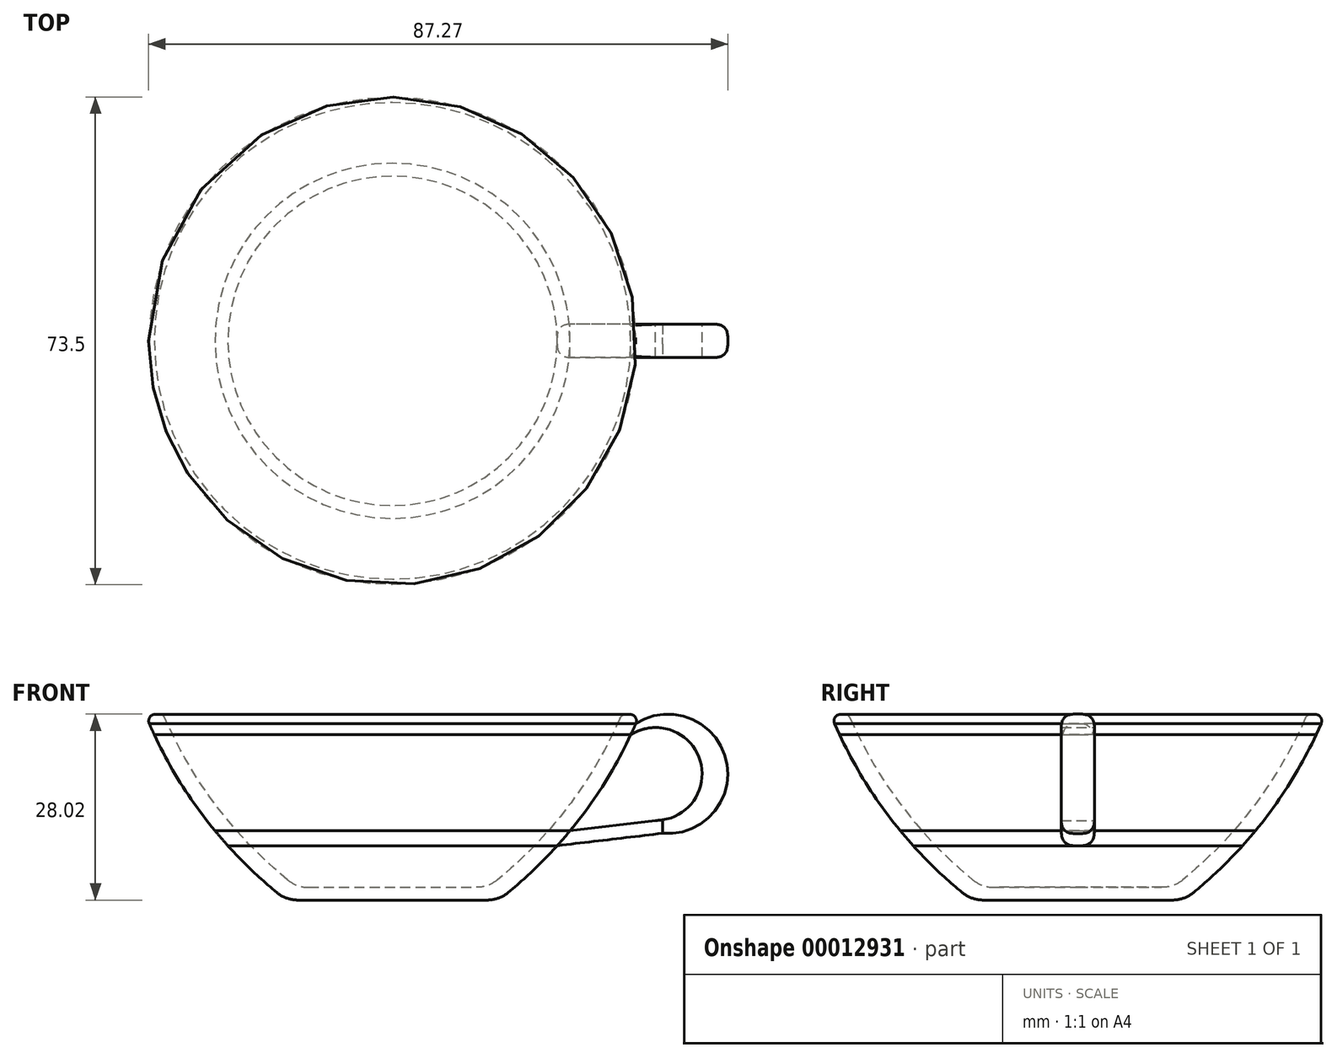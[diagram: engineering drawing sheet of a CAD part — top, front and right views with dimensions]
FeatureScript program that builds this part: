
annotation { "Feature Type Name" : "Feature", "Feature Type Description" : "" }
export const myFeature = defineFeature(function(context is Context, id is Id, definition is map)
    precondition{}
    {
        {
            var Q0;
            Q0=qCreatedBy(makeId("Front.planeOp"),FACE);
            var sketch = newSketch(context, id + "F0", { "sketchPlane" : qUnion([Q0])});
            skLineSegment(sketch, "E0", {"start": v(0, 0) * mm, "end": v(14.25, 0) * mm});
            skArc(sketch, "E1", {"start": v(17.42, 1.13) * mm, "mid": v(21.25, 4.52) * mm, "end": v(24.82, 8.2) * mm});
            skArc(sketch, "E2", {"start": v(15.8, 3.04) * mm, "mid": v(26.49, 14.13) * mm, "end": v(34.29, 27.4) * mm});
            skLineSegment(sketch, "E3", {"start": v(35.75, 28) * mm, "end": v(35.2, 28) * mm});
            skLineSegment(sketch, "E4", {"start": v(0, 0) * mm, "end": v(0, 1.91) * mm});
            skLineSegment(sketch, "E5", {"start": v(0, 1.91) * mm, "end": v(12.64, 1.91) * mm});
            skLineSegment(sketch, "E6", {"start": v(40.7, 10.06) * mm, "end": v(24.82, 8.2) * mm});
            skArc(sketch, "E7", {"start": v(39.61, 12) * mm, "mid": v(46.38, 20.94) * mm, "end": v(35.9, 24.9) * mm});
            skArc(sketch, "E8.trimOffspring", {"start": v(40.7, 10.06) * mm, "mid": v(50.26, 21.16) * mm, "end": v(36.66, 26.6) * mm});
            skLineSegment(sketch, "E9", {"start": v(39.61, 12) * mm, "end": v(26.76, 10.44) * mm});
            skPoint(sketch, "E10.visualSharp", {"position": v(37.25, 28) * mm});
            skArc(sketch, "E10.filletArc", {"start": v(36.66, 26.6) * mm, "mid": v(36.58, 27.55) * mm, "end": v(35.75, 28) * mm});
            skPoint(sketch, "E11.visualSharp", {"position": v(34.54, 28) * mm});
            skArc(sketch, "E11.filletArc", {"start": v(35.2, 28) * mm, "mid": v(34.65, 27.84) * mm, "end": v(34.29, 27.4) * mm});
            skPoint(sketch, "E12.visualSharp", {"position": v(16, 0) * mm});
            skArc(sketch, "E12.filletArc", {"start": v(14.25, 0) * mm, "mid": v(15.93, 0.3) * mm, "end": v(17.42, 1.13) * mm});
            skPoint(sketch, "E13.visualSharp", {"position": v(14.39, 1.91) * mm});
            skArc(sketch, "E13.filletArc", {"start": v(12.64, 1.91) * mm, "mid": v(14.32, 2.2) * mm, "end": v(15.8, 3.04) * mm});
            skArc(sketch, "E14.trimOffspring", {"start": v(26.76, 10.44) * mm, "mid": v(31.79, 17.39) * mm, "end": v(35.9, 24.9) * mm});
            skLineSegment(sketch, "E15", {"start": v(36.66, 26.6) * mm, "end": v(35.9, 24.9) * mm});
            skLineSegment(sketch, "E16", {"start": v(26.76, 10.44) * mm, "end": v(24.82, 8.2) * mm});
            skSolve(sketch);
        }
        {
            var Q0;
            {var subQ6=sQuery(id+"F0.wireOp",EDGE,"E0");Q0=makeQuery(id+"F0.imprint","IMPRINT",FACE,{"disambiguationData":[TD([[makeQuery(id+"F0.imprint","IMPRINT",EDGE,{"derivedFrom":subQ6}),1.0]])]});}
            var Q1;
            Q1=sQuery(id+"F0.wireOp",EDGE,"E4");
            revolve(context, id + "F1", {"entities" : qUnion([Q0]), "axis" : qUnion([Q1]), "revolveType" : RevolveType.FULL});
        }
        {
            var Q0;
            {var subQ3=sQuery(id+"F0.wireOp",EDGE,"E6");Q0=makeQuery(id+"F0.imprint","IMPRINT",FACE,{"disambiguationData":[TD([[makeQuery(id+"F0.imprint","IMPRINT",EDGE,{"derivedFrom":subQ3}),-1.0]])]});}
            extrude(context, id + "F2", {"entities" : qUnion([Q0]), "endBound" : BoundingType.SYMMETRIC, "depth" : 5 * mm});
        }
        {
            var Q0;
            Q0=makeQuery(id+"F2.opExtrude","CAP_EDGE",EDGE,{"disambiguationData":[OSD([sQuery(id+"F0.wireOp",EDGE,"E8.trimOffspring")])],"isStart":false});
            var Q1;
            Q1=makeQuery(id+"F2.opExtrude","CAP_EDGE",EDGE,{"disambiguationData":[OSD([sQuery(id+"F0.wireOp",EDGE,"E6")])],"isStart":false});
            var Q2;
            Q2=makeQuery(id+"F2.opExtrude","CAP_EDGE",EDGE,{"disambiguationData":[OSD([sQuery(id+"F0.wireOp",EDGE,"E8.trimOffspring")])],"isStart":true});
            var Q3;
            Q3=makeQuery(id+"F2.opExtrude","CAP_EDGE",EDGE,{"disambiguationData":[OSD([sQuery(id+"F0.wireOp",EDGE,"E6")])],"isStart":true});
            fillet(context, id + "F3", {"entities" : qUnion([Q0, Q1, Q2, Q3]), "radius" : 2 * mm, "tangentPropagation" : true, "rho" : 0.5, "crossSection" : FilletCrossSection.CONIC, "allowEdgeOverflow" : false});
        }
    });
